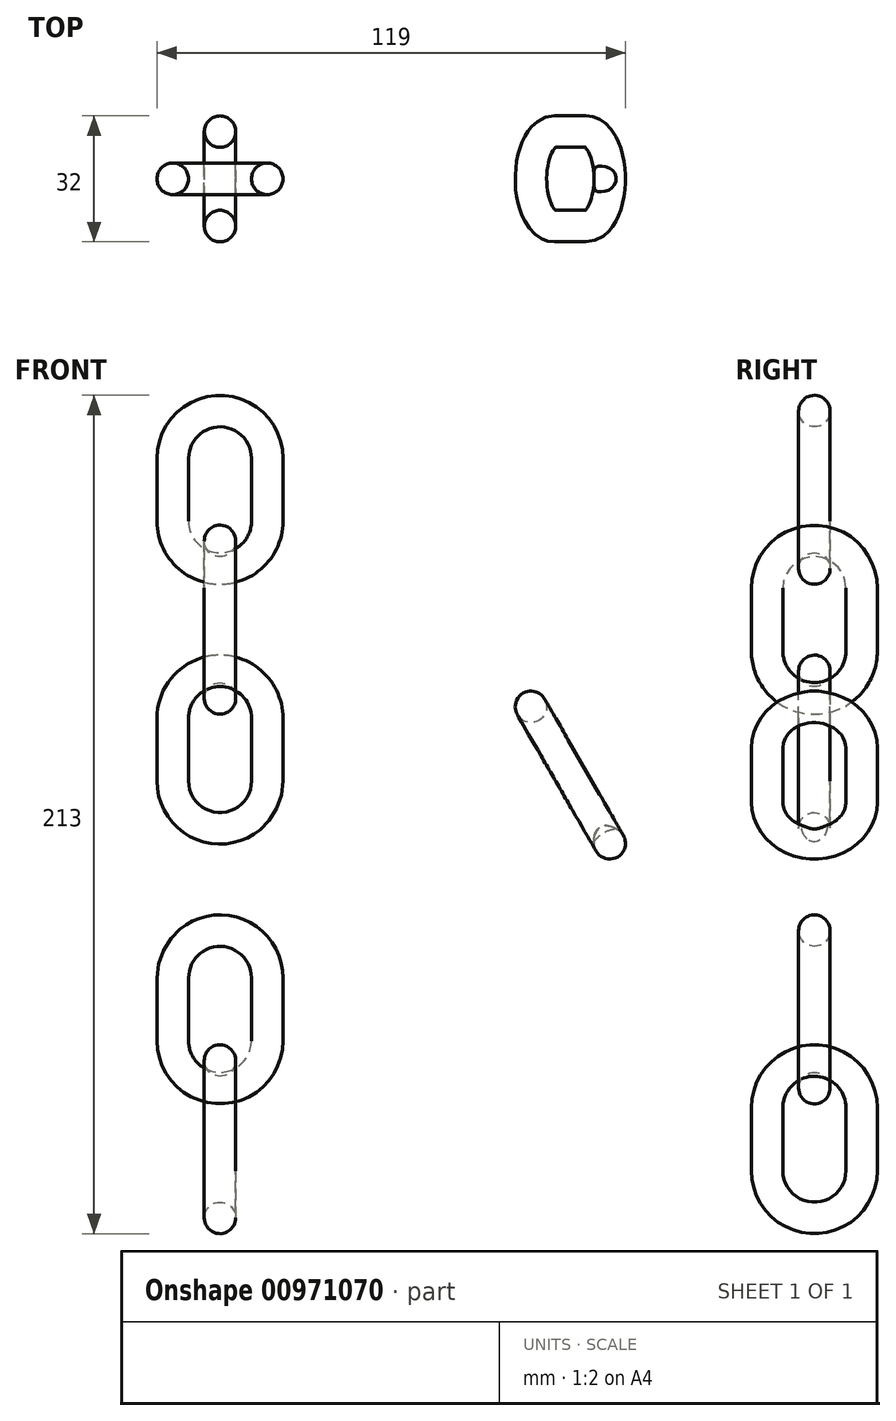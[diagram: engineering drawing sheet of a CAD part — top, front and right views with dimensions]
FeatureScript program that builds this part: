
annotation { "Feature Type Name" : "Feature", "Feature Type Description" : "" }
export const myFeature = defineFeature(function(context is Context, id is Id, definition is map)
    precondition{}
    {
        {
            var Q0;
            Q0=qCreatedBy(makeId("Top.planeOp"),FACE);
            var sketch = newSketch(context, id + "F0", { "sketchPlane" : qUnion([Q0])});
            skCircle(sketch, "E0", {"center": v(0, 12) * mm, "radius": 4 * mm});
            skSolve(sketch);
        }
        {
            var Q0;
            Q0=qCreatedBy(makeId("Right.planeOp"),FACE);
            var sketch = newSketch(context, id + "F1", { "sketchPlane" : qUnion([Q0])});
            skLineSegment(sketch, "E1.bottom", {"start": v(-12, -8) * mm, "end": v(12, -8) * mm, "construction": true});
            skLineSegment(sketch, "E1.top", {"start": v(-12, 8) * mm, "end": v(12, 8) * mm, "construction": true});
            skLineSegment(sketch, "E1.left", {"start": v(-12, -8) * mm, "end": v(-12, 8) * mm});
            skLineSegment(sketch, "E1.right", {"start": v(12, -8) * mm, "end": v(12, 8) * mm});
            skLineSegment(sketch, "E2", {"start": v(-12, -8) * mm, "end": v(0, 0) * mm, "construction": true});
            skLineSegment(sketch, "E3", {"start": v(0, 0) * mm, "end": v(12, -8) * mm, "construction": true});
            skArc(sketch, "E4", {"start": v(-12, -8) * mm, "mid": v(0, -20) * mm, "end": v(12, -8) * mm});
            skLineSegment(sketch, "E5", {"start": v(0, 0) * mm, "end": v(-12, 0) * mm, "construction": true});
            skArc(sketch, "E6.MirrorCS", {"start": v(-12, 8) * mm, "mid": v(0, 20) * mm, "end": v(12, 8) * mm});
            skSolve(sketch);
        }
        {
            var Q0;
            Q0=makeQuery(id+"F0.imprint","IMPRINT",FACE,{"disambiguationData":[TD([[makeQuery(id+"F0.imprint","IMPRINT",EDGE,{"derivedFrom":sQuery(id+"F0.wireOp",EDGE,"E0")}),1.0]])]});
            var Q1;
            Q1=sQuery(id+"F1.wireOp",EDGE,"E1.right");
            var Q2;
            Q2=sQuery(id+"F1.wireOp",EDGE,"E4");
            var Q3;
            Q3=sQuery(id+"F1.wireOp",EDGE,"E1.left");
            var Q4;
            Q4=sQuery(id+"F1.wireOp",EDGE,"E6.MirrorCS");
            sweep(context, id + "F2", {"profiles" : qUnion([Q0]), "path" : qUnion([Q1, Q2, Q3, Q4])});
        }
        {
            var Q0;
            Q0=makeQuery(id+"F2.opSweep","SWEPT_BODY",BODY,{"disambiguationData":[OSD([sQuery(id+"F0.wireOp",EDGE,"E0"),sQuery(id+"F1.wireOp",EDGE,"E4")])]});
            transform(context, id + "F3", {"entities" : qUnion([Q0]), "transformType" : TransformType.TRANSLATION_3D, "dx" : 0 * mm, "dy" : 0 * mm, "dz" : 33 * mm, "makeCopy" : true});
        }
        {
            var Q0;
            Q0=qCreatedBy(makeId("Right.planeOp"),FACE);
            var sketch = newSketch(context, id + "F4", { "sketchPlane" : qUnion([Q0])});
            skLineSegment(sketch, "E7", {"start": v(0, 0) * mm, "end": v(0, 71.54) * mm, "construction": true});
            skSolve(sketch);
        }
        {
            var Q0;
            Q0=makeQuery(id+"F3.opPattern","COPY",BODY,{"derivedFrom":makeQuery(id+"F2.opSweep","SWEPT_BODY",BODY,{"disambiguationData":[OSD([sQuery(id+"F0.wireOp",EDGE,"E0"),sQuery(id+"F1.wireOp",EDGE,"E4")])]}),"instanceName":"1"});
            var Q1;
            Q1=sQuery(id+"F4.wireOp",EDGE,"E7");
            transform(context, id + "F5", {"entities" : qUnion([Q0]), "transformType" : TransformType.ROTATION, "transformAxis" : qUnion([Q1]), "angle" : 90 * degree, "makeCopy" : false});
        }
        {
            var Q0;
            Q0=makeQuery(id+"F3.opPattern","COPY",BODY,{"derivedFrom":makeQuery(id+"F2.opSweep","SWEPT_BODY",BODY,{"disambiguationData":[OSD([sQuery(id+"F0.wireOp",EDGE,"E0"),sQuery(id+"F1.wireOp",EDGE,"E4")])]}),"instanceName":"1"});
            transform(context, id + "F6", {"entities" : qUnion([Q0]), "transformType" : TransformType.TRANSLATION_3D, "dx" : 0 * mm, "dy" : 0 * mm, "dz" : 66 * mm, "makeCopy" : true});
        }
        {
            var Q0;
            Q0=makeQuery(id+"F3.opPattern","COPY",BODY,{"derivedFrom":makeQuery(id+"F2.opSweep","SWEPT_BODY",BODY,{"disambiguationData":[OSD([sQuery(id+"F0.wireOp",EDGE,"E0"),sQuery(id+"F1.wireOp",EDGE,"E4")])]}),"instanceName":"1"});
            transform(context, id + "F7", {"entities" : qUnion([Q0]), "transformType" : TransformType.TRANSLATION_3D, "dx" : 0 * mm, "dy" : 0 * mm, "dz" : 132 * mm, "makeCopy" : true});
        }
        {
            var Q0;
            Q0=makeQuery(id+"F3.opPattern","COPY",BODY,{"derivedFrom":makeQuery(id+"F2.opSweep","SWEPT_BODY",BODY,{"disambiguationData":[OSD([sQuery(id+"F0.wireOp",EDGE,"E0"),sQuery(id+"F1.wireOp",EDGE,"E4")])]}),"instanceName":"1"});
            transform(context, id + "F8", {"entities" : qUnion([Q0]), "transformType" : TransformType.TRANSLATION_3D, "dx" : 0 * mm, "dy" : 0 * mm, "dz" : 66 * mm, "makeCopy" : true});
        }
        {
            var Q0;
            Q0=makeQuery(id+"F3.opPattern","COPY",BODY,{"derivedFrom":makeQuery(id+"F2.opSweep","SWEPT_BODY",BODY,{"disambiguationData":[OSD([sQuery(id+"F0.wireOp",EDGE,"E0"),sQuery(id+"F1.wireOp",EDGE,"E4")])]}),"instanceName":"1"});
            var Q1;
            Q1=makeQuery(id+"F8.opPattern","COPY",BODY,{"derivedFrom":makeQuery(id+"F3.opPattern","COPY",BODY,{"derivedFrom":makeQuery(id+"F2.opSweep","SWEPT_BODY",BODY,{"disambiguationData":[OSD([sQuery(id+"F0.wireOp",EDGE,"E0"),sQuery(id+"F1.wireOp",EDGE,"E4")])]}),"instanceName":"1"}),"instanceName":"1"});
            booleanBodies(context, id + "F9", {"operationType" : BooleanOperationType.SUBTRACTION, "tools" : qUnion([Q0]), "targets" : qUnion([Q1]), "keepTools" : true});
        }
        {
            var Q0;
            Q0=makeQuery(id+"F8.opPattern","COPY",BODY,{"derivedFrom":makeQuery(id+"F3.opPattern","COPY",BODY,{"derivedFrom":makeQuery(id+"F2.opSweep","SWEPT_BODY",BODY,{"disambiguationData":[OSD([sQuery(id+"F0.wireOp",EDGE,"E0"),sQuery(id+"F1.wireOp",EDGE,"E4")])]}),"instanceName":"1"}),"instanceName":"1"});
            transform(context, id + "F10", {"entities" : qUnion([Q0]), "transformType" : TransformType.TRANSLATION_3D, "dx" : 0 * mm, "dy" : 0 * mm, "dz" : 33 * mm, "makeCopy" : true});
        }
        {
            var Q0;
            Q0=makeQuery(id+"F10.opPattern","COPY",BODY,{"derivedFrom":makeQuery(id+"F8.opPattern","COPY",BODY,{"derivedFrom":makeQuery(id+"F3.opPattern","COPY",BODY,{"derivedFrom":makeQuery(id+"F2.opSweep","SWEPT_BODY",BODY,{"disambiguationData":[OSD([sQuery(id+"F0.wireOp",EDGE,"E0"),sQuery(id+"F1.wireOp",EDGE,"E4")])]}),"instanceName":"1"}),"instanceName":"1"}),"instanceName":"1"});
            var Q1;
            Q1=sQuery(id+"F4.wireOp",EDGE,"E7");
            transform(context, id + "F11", {"entities" : qUnion([Q0]), "transformType" : TransformType.ROTATION, "transformAxis" : qUnion([Q1]), "angle" : 90 * degree, "makeCopy" : false});
        }
        {
            var Q0;
            Q0=makeQuery(id+"F3.opPattern","COPY",BODY,{"derivedFrom":makeQuery(id+"F2.opSweep","SWEPT_BODY",BODY,{"disambiguationData":[OSD([sQuery(id+"F0.wireOp",EDGE,"E0"),sQuery(id+"F1.wireOp",EDGE,"E4")])]}),"instanceName":"1"});
            transform(context, id + "F12", {"entities" : qUnion([Q0]), "transformType" : TransformType.TRANSLATION_3D, "dx" : 0 * mm, "dy" : 0 * mm, "dz" : 264 * mm, "makeCopy" : true});
        }
        {
            var Q0;
            Q0=makeQuery(id+"F12.opPattern","COPY",BODY,{"derivedFrom":makeQuery(id+"F3.opPattern","COPY",BODY,{"derivedFrom":makeQuery(id+"F2.opSweep","SWEPT_BODY",BODY,{"disambiguationData":[OSD([sQuery(id+"F0.wireOp",EDGE,"E0"),sQuery(id+"F1.wireOp",EDGE,"E4")])]}),"instanceName":"1"}),"instanceName":"1"});
            var Q1;
            Q1=makeQuery(id+"F3.opPattern","COPY",BODY,{"derivedFrom":makeQuery(id+"F2.opSweep","SWEPT_BODY",BODY,{"disambiguationData":[OSD([sQuery(id+"F0.wireOp",EDGE,"E0"),sQuery(id+"F1.wireOp",EDGE,"E4")])]}),"instanceName":"1"});
            booleanBodies(context, id + "F13", {"operationType" : BooleanOperationType.SUBTRACTION, "tools" : qUnion([Q0]), "targets" : qUnion([Q1])});
        }
        {
            var Q0;
            Q0=makeQuery(id+"F3.opPattern","COPY",BODY,{"derivedFrom":makeQuery(id+"F2.opSweep","SWEPT_BODY",BODY,{"disambiguationData":[OSD([sQuery(id+"F0.wireOp",EDGE,"E0"),sQuery(id+"F1.wireOp",EDGE,"E4")])]}),"instanceName":"1"});
            transform(context, id + "F14", {"entities" : qUnion([Q0]), "transformType" : TransformType.TRANSLATION_3D, "dx" : 0 * mm, "dy" : 0 * mm, "dz" : 66 * mm, "makeCopy" : true});
        }
        {
            var Q0;
            Q0=makeQuery(id+"F3.opPattern","COPY",BODY,{"derivedFrom":makeQuery(id+"F2.opSweep","SWEPT_BODY",BODY,{"disambiguationData":[OSD([sQuery(id+"F0.wireOp",EDGE,"E0"),sQuery(id+"F1.wireOp",EDGE,"E4")])]}),"instanceName":"1"});
            var Q1;
            Q1=makeQuery(id+"F14.opPattern","COPY",BODY,{"derivedFrom":makeQuery(id+"F3.opPattern","COPY",BODY,{"derivedFrom":makeQuery(id+"F2.opSweep","SWEPT_BODY",BODY,{"disambiguationData":[OSD([sQuery(id+"F0.wireOp",EDGE,"E0"),sQuery(id+"F1.wireOp",EDGE,"E4")])]}),"instanceName":"1"}),"instanceName":"1"});
            booleanBodies(context, id + "F15", {"operationType" : BooleanOperationType.SUBTRACTION, "tools" : qUnion([Q0]), "targets" : qUnion([Q1]), "keepTools" : true});
        }
        {
            var Q0;
            Q0=makeQuery(id+"F14.opPattern","COPY",BODY,{"derivedFrom":makeQuery(id+"F3.opPattern","COPY",BODY,{"derivedFrom":makeQuery(id+"F2.opSweep","SWEPT_BODY",BODY,{"disambiguationData":[OSD([sQuery(id+"F0.wireOp",EDGE,"E0"),sQuery(id+"F1.wireOp",EDGE,"E4")])]}),"instanceName":"1"}),"instanceName":"1"});
            var Q1;
            Q1=sQuery(id+"F4.wireOp",EDGE,"E7");
            transform(context, id + "F16", {"entities" : qUnion([Q0]), "transformType" : TransformType.ROTATION, "transformAxis" : qUnion([Q1]), "angle" : 90 * degree, "makeCopy" : false});
        }
        {
            var Q0;
            Q0=makeQuery(id+"F14.opPattern","COPY",BODY,{"derivedFrom":makeQuery(id+"F3.opPattern","COPY",BODY,{"derivedFrom":makeQuery(id+"F2.opSweep","SWEPT_BODY",BODY,{"disambiguationData":[OSD([sQuery(id+"F0.wireOp",EDGE,"E0"),sQuery(id+"F1.wireOp",EDGE,"E4")])]}),"instanceName":"1"}),"instanceName":"1"});
            transform(context, id + "F17", {"entities" : qUnion([Q0]), "transformType" : TransformType.TRANSLATION_3D, "dx" : 0 * mm, "dy" : 0 * mm, "dz" : -33 * mm, "makeCopy" : false});
        }
        {
            var Q0;
            Q0=makeQuery(id+"F3.opPattern","COPY",BODY,{"derivedFrom":makeQuery(id+"F2.opSweep","SWEPT_BODY",BODY,{"disambiguationData":[OSD([sQuery(id+"F0.wireOp",EDGE,"E0"),sQuery(id+"F1.wireOp",EDGE,"E4")])]}),"instanceName":"1"});
            var Q1;
            Q1=makeQuery(id+"F14.opPattern","COPY",BODY,{"derivedFrom":makeQuery(id+"F3.opPattern","COPY",BODY,{"derivedFrom":makeQuery(id+"F2.opSweep","SWEPT_BODY",BODY,{"disambiguationData":[OSD([sQuery(id+"F0.wireOp",EDGE,"E0"),sQuery(id+"F1.wireOp",EDGE,"E4")])]}),"instanceName":"1"}),"instanceName":"1"});
            booleanBodies(context, id + "F18", {"operationType" : BooleanOperationType.SUBTRACTION, "tools" : qUnion([Q0]), "targets" : qUnion([Q1]), "keepTools" : true});
        }
        {
            var Q0;
            Q0=qCreatedBy(makeId("Right.planeOp"),FACE);
            var sketch = newSketch(context, id + "F19", { "sketchPlane" : qUnion([Q0])});
            skLineSegment(sketch, "E8", {"start": v(100, 264) * mm, "end": v(-100, 264) * mm, "construction": true});
            skLineSegment(sketch, "E9", {"start": v(0, 272) * mm, "end": v(0, 256) * mm, "construction": true});
            skLineSegment(sketch, "E10", {"start": v(100, 264) * mm, "end": v(0, 264) * mm, "construction": true});
            skSolve(sketch);
        }
        {
            var Q0;
            Q0=makeQuery(id+"F14.opPattern","COPY",BODY,{"derivedFrom":makeQuery(id+"F3.opPattern","COPY",BODY,{"derivedFrom":makeQuery(id+"F2.opSweep","SWEPT_BODY",BODY,{"disambiguationData":[OSD([sQuery(id+"F0.wireOp",EDGE,"E0"),sQuery(id+"F1.wireOp",EDGE,"E4")])]}),"instanceName":"1"}),"instanceName":"1"});
            var Q1;
            Q1=sQuery(id+"F19.wireOp",EDGE,"E8");
            transform(context, id + "F20", {"entities" : qUnion([Q0]), "transformType" : TransformType.ROTATION, "transformAxis" : qUnion([Q1]), "angle" : 30 * degree, "makeCopy" : false});
        }
        {
            var Q0;
            Q0=makeQuery(id+"F14.opPattern","COPY",BODY,{"derivedFrom":makeQuery(id+"F3.opPattern","COPY",BODY,{"derivedFrom":makeQuery(id+"F2.opSweep","SWEPT_BODY",BODY,{"disambiguationData":[OSD([sQuery(id+"F0.wireOp",EDGE,"E0"),sQuery(id+"F1.wireOp",EDGE,"E4")])]}),"instanceName":"1"}),"instanceName":"1"});
            transform(context, id + "F21", {"entities" : qUnion([Q0]), "transformType" : TransformType.TRANSLATION_3D, "dx" : -10 * mm, "dy" : 0 * mm, "dz" : 0 * mm, "makeCopy" : false});
        }
    });
